# Revit family: PRD_AR_JntrlUnits_SiriusMultiPurposeSink_BS315N
name_source: partatom
category: Plumbing Fixtures
revit_build: Autodesk Revit 2018 (Build: 20190510_1515(x64)
units: mm (PartAtom-declared; Revit-internal decimal feet)

## family parameters
Cut with Voids When Loaded = No
Host = Face
OmniClass Number = 23.45.05.14.14
OmniClass Title = Sinks/Lavatories
Part Type = Normal
Room Calculation Point = No
Round Connector Dimension = Use Diameter
Shared = No

## types (1)
- BS315N
    AssetType = Fixed
    BIMObjectName = PRD_AR_JanitorialUnits_SiriusMultiPurposeSink_BS315N
    Category = Pr_40_20_96_44, Janitorial sinks
    Color = Stainless steel
    Default Elevation = 850 mm  [stored 2.78871 ft]
    Description = SIRIUS washtrough with 2 basins for wall mounting, stainless steel, satin finished surface, material thickness of trough 0.8 mm / side panels 1.2 mm, seamlessly welded side panels with integrated wall brackets, front panel with rubbing board, 70 mm lowered tap landing, no overflow, 40 mm rear upstand, 2 central wastes, G 1 1/2 B plastic standpipe strainers (x2), removable corner protection plates, includes fixings.
    DrainSize = DN 40 (1 1/2 inch.)
    DurationUnit = year
    Features = stainless steel, 0.80 mm, satin finished, wall mounting, 1420x346x500 mm (WxHxD)
    Finish = Satin finished
    FinishAndMaterial = Stainless steel 1.4301
    Form = Stainless steel multi purpose sink
    GrossWeight = 15.20 kg
    IfcExportAs = IfcSanitaryTerminalType
    IfcExportType = SINK
    IntegralAccessories = incl. stainless steel screws and dowels
    Manufacturer = KWC Group AG
    ManufacturerName = KWC Group AG
    ManufacturerURL = www.kwc.com
    Material = Stainless steel
    Model = BS315N
    ModelNumber = 2030045755
    ModelReference = BS315N
    NBSDescription = Janitorial units
    NBSReference = 45-35-70/401
    Name = Sirius multi purpose sink BS315N
    NetWeight = 13.50 kg
    NominalDepth = 500 mm  [stored 1.64042 ft]
    NominalHeight = 346 mm  [stored 1.13517 ft]
    NominalWidth = 1420 mm  [stored 4.65879 ft]
    OutletSize = DN 40 (1 1/2 inch.)
    ProductInformation = https://pim.kwc.com
    Shape = Rectangular
    SinkMaterial = PRD_AR_StainlessSteel_SatinFinished
    SinkMounting = WallHung
    SinkType = Other
    Size = 1420 x 500 x 346 mm
    URL = www.kwc.com
    Uniclass2015Code = Pr_40_20_96_44
    Uniclass2015Title = Janitorial sinks
    Uniclass2015Version = Products v1.10
    Version = 1
    WarrantyDurationUnit = year
    WasteSize = 40  [stored 0.131234 ft]
    WaterSupplyOverflowAndWasteHolesOverflow = Stand pipe overflow
    WaterSupplyOverflowAndWasteHolesWaste = Right-Back-Corner
    WaterSupplyOverflowAndWasteHolesWaterSupply = No tapholes

note: [stored X ft] marks values corroborated as IEEE doubles in the binary element streams (Revit-internal decimal feet)

## geometry (parser evidence)
native form markers: Sweep x6
no freeform markers — native parametric forms only
